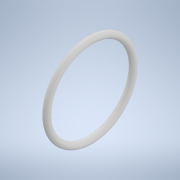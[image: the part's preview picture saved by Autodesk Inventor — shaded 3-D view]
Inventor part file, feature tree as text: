
AUTODESK INVENTOR PART (.ipt)
format: ipt  version: 2021 (Build 250183000, 183)  size: 122,368 bytes
history: native  units: mm
features: revolve x1, sketch x1
ambient origin geometry x8: Origin, YZ Plane, XZ Plane, XY Plane, X Axis, Y Axis, Z Axis, Center Point
bodies: Solid1 (feature_tree)
feature tree (2):
  revolve  "Revolution1"  [1 undecoded]
  sketch  "Sketch1"  dims[d0=5.0mm d1=33.0mm d2=90.0deg]
note: 1 required parameter value undecoded (feature->parameter linkage not recoverable at this tier; creation-order binding heuristic only, values carry confidence <= 0.55)
